# Revit family: Hager-Madrid-IP65-D250-Cl.I-Steel_encl-630A-NoHosted-IT-it
name_source: partatom
category: Electrical Equipment
units: mm (PartAtom-declared; Revit-internal decimal feet)

## family parameters
Always vertical = Yes
Cut with Voids When Loaded = No
Panel Configuration = Two Columns, Circuits Across
Part Type = Panelboard
Room Calculation Point = No
Round Connector Dimension = Use Diameter
Shared = No
Work Plane-Based = Yes

## types (11) — shared parameters
Default Elevation = 1219 mm
EF000003 - Tipo di montaggio = EV000384 - A parete
EF000007 - colore = EV000270 - grigio
EF000049 - profondità = 250 mm  [stored 0.82021 ft]
EF000116 - numero RAL = 7035
EF000118 - con piastra di montaggio = Yes
EF000339 - tipo di copertura = EV004216 - porta
EF001088 - possibilità di applicazione = Yes
EF001131 - profondità interna = 250 mm  [stored 0.82021 ft]
EF001596 - Attacco Lampada = EV000179 - acciaio
EF001613 - Integrità del circuito = EV000494 - senza
EF003532 - adatto per uso esterno = No
EF004293 - resistenza agli urti = EV008784 - IK10
EF004464 - tipo di porta = EV002646 - singolo
EF005474 - grado di protezione (IP) = EV006421 - IP65
EF007800 - adatto per parafulmine = No
EF008873 - corrente nominale (In) = 630 A
EF009170 - spessore materiale scatola = 1 mm  [stored 0.00328084 ft]
EF009171 - spessore materiale porta/coperchio = 2 mm  [stored 0.00656168 ft]
EF009212 - esecuzione coperchio = EV000116 - chiuso
EF015940 - Coprire con rilascio di sovrapressione = No
HG000002 - Con porta = Yes
HG000003 - Gamma = Madrid
HG000006 - Ad incasso = No
HG000009 - Porta doppia a battente = No
HG000010 - Porte asimmetriche = No
HG000023 - Custodia a doppia sezione = No
HG000024 - Altezza della sezione inferiore = 600 mm
HG000026 - A pavimento = No
Manufacturer = Hager
Type Comments = Madrid
zero-valued in all types: EF000218 - profondità di incasso, EF002950 - Numero moduli DIN, EF004427 - numero di moduli, HG000027 - Altezza dello zoccolo

## per-type parameters (varying)
| type | EF000008 - Larghezza | EF000040 - Altezza | EF000266 - numero di file | EF000437 - numero di ingressi per conduttori | EF006244 - coperchio/porta trasparente | EF006306 - con serratura | EF009554 - numero delle aperture per la piastra della flangia | HG000004 - Codice produttore |
| A parete IP65 L400 A600 P250  - 35715 | 400 mm  [stored 1.31234 ft] | 600 mm | 0 | 0 | No | Yes | 0 | 35715 |
| A parete IP65 L400 A600 P250  - 35765 | 400 mm  [stored 1.31234 ft] | 600 mm | 0 | 2 | Yes | No | 2 | 35765 |
| A parete IP65 L500 A650 P250  - 35721 | 500 mm  [stored 1.64042 ft] | 650 mm  [stored 2.13255 ft] | 1 | 2 | No | Yes | 2 | 35721 |
| A parete IP65 L500 A650 P250  - 35771 | 500 mm  [stored 1.64042 ft] | 650 mm  [stored 2.13255 ft] | 4 | 2 | Yes | No | 2 | 35771 |
| A parete IP65 L600 A1250 P250  - 35739 | 600 mm | 1250 mm  [stored 4.10105 ft] | 8 | 2 | No | Yes | 2 | 35739 |
| A parete IP65 L600 A1250 P250  - 35789 | 600 mm | 1250 mm  [stored 4.10105 ft] | 8 | 2 | Yes | No | 2 | 35789 |
| A parete IP65 L600 A600 P250  - 35717 | 600 mm | 600 mm | 0 | 2 | No | Yes | 2 | 35717 |
| A parete IP65 L600 A600 P250  - 35767 | 600 mm | 600 mm | 0 | 2 | Yes | No | 2 | 35767 |
| A parete IP65 L600 A800 P250  - 35728 | 600 mm | 800 mm  [stored 2.62467 ft] | 1 | 2 | No | Yes | 2 | 35728 |
| A parete IP65 L600 A800 P250  - 35778 | 600 mm | 800 mm  [stored 2.62467 ft] | 5 | 2 | Yes | No | 2 | 35778 |
| A parete IP65 L800 A950 P250  - 35736 | 800 mm  [stored 2.62467 ft] | 950 mm  [stored 3.1168 ft] | 1 | 2 | No | Yes | 2 | 35736 |

note: [stored X ft] marks values corroborated as IEEE doubles in the binary element streams (Revit-internal decimal feet)

## geometry (parser evidence)
native form markers: Blend x4, Sweep x9
no freeform markers — native parametric forms only
